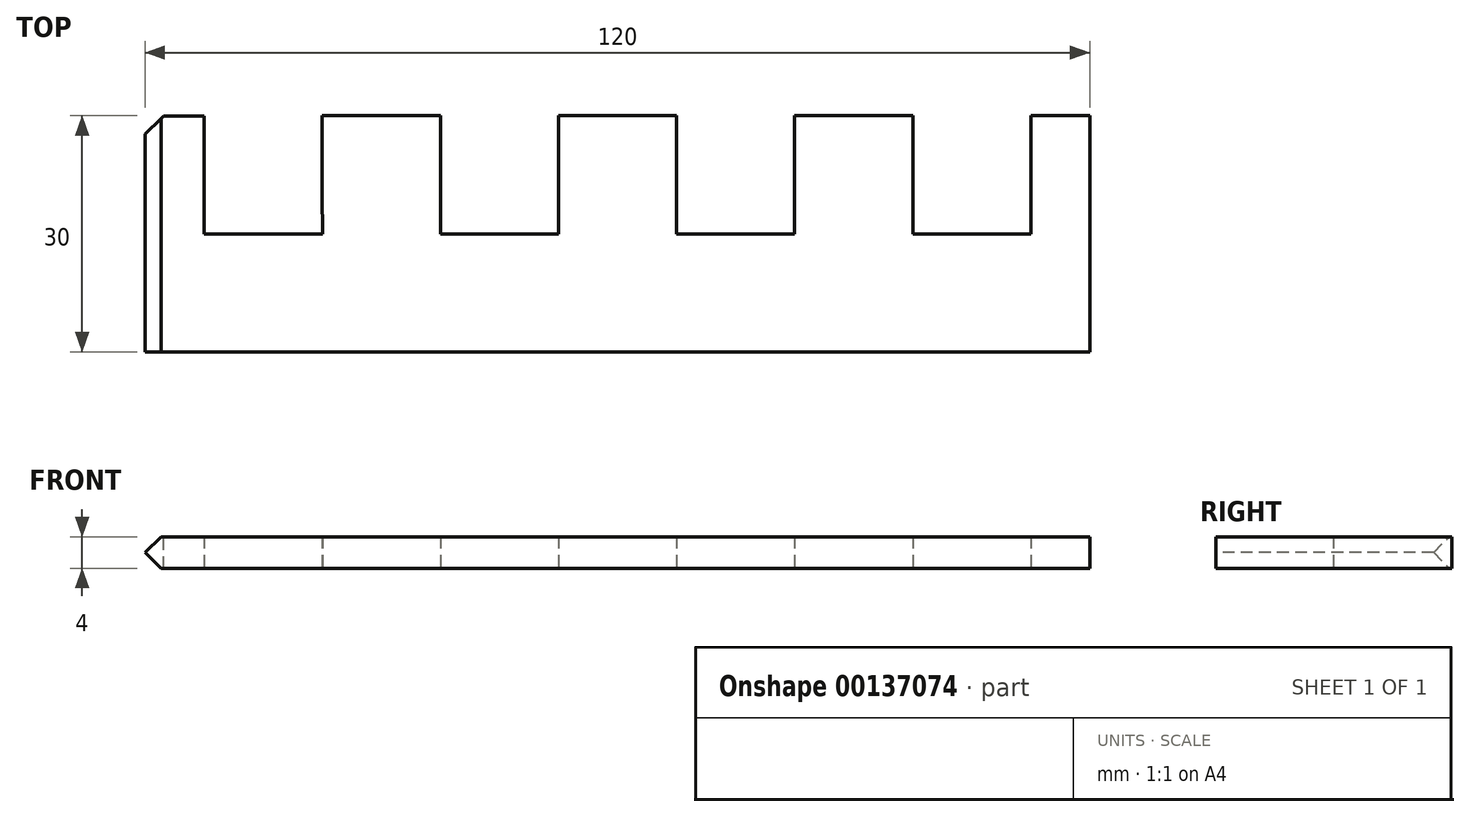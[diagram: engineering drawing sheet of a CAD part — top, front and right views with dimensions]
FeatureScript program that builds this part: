
annotation { "Feature Type Name" : "Feature", "Feature Type Description" : "" }
export const myFeature = defineFeature(function(context is Context, id is Id, definition is map)
    precondition{}
    {
        {
            var Q0;
            Q0=qCreatedBy(makeId("Top.planeOp"),FACE);
            var sketch = newSketch(context, id + "F0", { "sketchPlane" : qUnion([Q0])});
            skLineSegment(sketch, "E0", {"start": v(-75.44, -30) * mm, "end": v(44.56, -30) * mm});
            skLineSegment(sketch, "E1", {"start": v(44.56, -30) * mm, "end": v(44.56, 0) * mm});
            skLineSegment(sketch, "E2", {"start": v(-67.95, -0.08) * mm, "end": v(-67.95, -10.08) * mm});
            skLineSegment(sketch, "E3", {"start": v(-52.95, 0) * mm, "end": v(-52.95, -10) * mm});
            skLineSegment(sketch, "E4", {"start": v(-37.95, 0) * mm, "end": v(-37.95, -10) * mm});
            skLineSegment(sketch, "E5", {"start": v(-22.95, 0) * mm, "end": v(-22.95, -10) * mm});
            skLineSegment(sketch, "E6", {"start": v(-7.95, 0) * mm, "end": v(-7.94, -10) * mm});
            skLineSegment(sketch, "E7", {"start": v(7.06, 0) * mm, "end": v(7.06, -10) * mm});
            skLineSegment(sketch, "E8", {"start": v(22.06, 0) * mm, "end": v(22.06, -10) * mm});
            skLineSegment(sketch, "E9", {"start": v(37.06, 0) * mm, "end": v(37.06, -10) * mm});
            skLineSegment(sketch, "E10", {"start": v(-52.95, 0) * mm, "end": v(-37.95, 0) * mm});
            skLineSegment(sketch, "E11", {"start": v(-22.95, 0) * mm, "end": v(-7.95, 0) * mm});
            skLineSegment(sketch, "E12", {"start": v(7.06, 0) * mm, "end": v(22.06, 0) * mm});
            skLineSegment(sketch, "E13", {"start": v(37.06, 0) * mm, "end": v(44.56, 0) * mm});
            skLineSegment(sketch, "E14", {"start": v(-75.44, -15.06) * mm, "end": v(-75.44, -30) * mm});
            skLineSegment(sketch, "E15", {"start": v(-67.95, -10.08) * mm, "end": v(-67.92, -15.06) * mm});
            skLineSegment(sketch, "E16", {"start": v(-52.95, -10) * mm, "end": v(-52.92, -15.06) * mm});
            skLineSegment(sketch, "E17", {"start": v(-37.95, -10) * mm, "end": v(-37.95, -15.06) * mm});
            skLineSegment(sketch, "E18", {"start": v(-22.95, -10) * mm, "end": v(-22.95, -15.06) * mm});
            skLineSegment(sketch, "E19", {"start": v(-7.94, -10) * mm, "end": v(-7.94, -15.06) * mm});
            skLineSegment(sketch, "E20", {"start": v(7.06, -10) * mm, "end": v(7.06, -15.06) * mm});
            skLineSegment(sketch, "E21", {"start": v(22.06, -10) * mm, "end": v(22.06, -15.06) * mm});
            skLineSegment(sketch, "E22", {"start": v(37.06, -10) * mm, "end": v(37.06, -15.06) * mm});
            skLineSegment(sketch, "E23", {"start": v(-67.92, -15.06) * mm, "end": v(-52.92, -15.06) * mm});
            skLineSegment(sketch, "E24", {"start": v(-37.95, -15.06) * mm, "end": v(-22.95, -15.06) * mm});
            skLineSegment(sketch, "E25", {"start": v(-7.94, -15.06) * mm, "end": v(7.06, -15.06) * mm});
            skLineSegment(sketch, "E26", {"start": v(22.06, -15.06) * mm, "end": v(37.06, -15.06) * mm});
            skLineSegment(sketch, "E27", {"start": v(-75.44, -30) * mm, "end": v(-75.44, -28.67) * mm});
            skLineSegment(sketch, "E28", {"start": v(-75.44, 0) * mm, "end": v(-75.44, -30) * mm});
            skLineSegment(sketch, "E29", {"start": v(-75.44, 0) * mm, "end": v(-67.95, -0.08) * mm});
            skSolve(sketch);
        }
        {
            var Q0;
            Q0 = qSketchRegion(id + "F0", true);
            extrude(context, id + "F1", {"entities" : qUnion([Q0]), "depth" : 4 * mm});
        }
        {
            var Q0;
            Q0=makeQuery(id+"F1.opExtrude","SWEPT_EDGE",EDGE,{"disambiguationData":[OSD([sQuery(id+"F0.wireOp",EDGE,"E28"),sQuery(id+"F0.wireOp",EDGE,"E29")])]});
            chamfer(context, id + "F2", {"entities" : qUnion([Q0]), "width" : 2.3 * mm, "tangentPropagation" : true});
        }
        {
            var Q0;
            Q0=makeQuery(id+"F1.opExtrude","CAP_EDGE",EDGE,{"disambiguationData":[OSD([sQuery(id+"F0.wireOp",EDGE,"E28")])],"isStart":true});
            var Q1;
            Q1=makeQuery(id+"F1.opExtrude","CAP_EDGE",EDGE,{"disambiguationData":[OSD([sQuery(id+"F0.wireOp",EDGE,"E28")])],"isStart":false});
            chamfer(context, id + "F3", {"entities" : qUnion([Q0, Q1]), "width" : 2 * mm, "tangentPropagation" : true});
        }
    });
